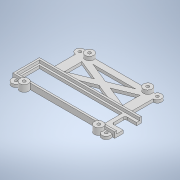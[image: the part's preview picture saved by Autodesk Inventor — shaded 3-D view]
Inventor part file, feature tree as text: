
AUTODESK INVENTOR PART (.ipt)
format: ipt  version: 2020.4 (Build 244396000, 396)  size: 266,752 bytes
history: native  units: mm
features: reference x19, other x9, extrude x4, sketch x4, fillet x1
ambient origin geometry x8: Origin, YZ Plane, XZ Plane, XY Plane, X Axis, Y Axis, Z Axis, Center Point
bodies: Solid1 (feature_tree)
feature tree (37):
  extrude  "Extrusion1"  Depth=2.0mm
  extrude  "Extrusion2"  Depth=3.0mm
  extrude  "Extrusion3"  Depth=3.0mm
  extrude  "Extrusion4"  Depth=3.0mm
  fillet  "Fillet1"  Radius=3.0mm
  sketch  "Sketch1"  dims[d0=2.0mm d1=2.0mm]
  reference  "Reference1"
  reference  "Reference2"
  reference  "Reference3"
  reference  "Reference4"
  reference  "Reference5"
  reference  "Reference6"
  reference  "Reference7"
  reference  "Reference8"
  reference  "Reference9"
  sketch  "Sketch2"  dims[d2=3.0mm d3=3.0mm]
  reference  "Reference10"
  reference  "Reference11"
  reference  "Reference12"
  reference  "Reference13"
  sketch  "Sketch3"  dims[d4=3.0mm d5=3.0mm]
  reference  "Reference14"
  reference  "Reference15"
  reference  "Reference16"
  reference  "Reference17"
  reference  "Reference18"
  reference  "Reference19"
  sketch  "Sketch4"  dims[d6=3.0mm d7=3.0mm d8=3.0mm d9=3.0mm d10=6.199922mm d11=6.199922mm d12=6.199922mm d13=3.099961mm d14=3.099961mm d15=3.0mm d16=0.0mm d18=3.0mm d19=0.0mm d20=4.0mm d21=0.0mm d22=8.0mm d23=4.0mm d24=4.0mm d25=4.0mm d26=9.0mm d27=5.0mm d28=10.0mm d29=0.0mm d30=2.0mm]
  other  "<userpath>\Dokumentumok\BME\Dipterv\3d\robot_v2_turnigy.iam"
  other  "robot_v2_turnigy.iam"
  other  "turnigy_battery:1"
  other  "electronics:1"
  other  "main_board:1"
  other  "PCB Component:1"
  other  "Board:1"
  other  "bottom2_turnigy:1"
  other  "tavtarto_30mm:4"
